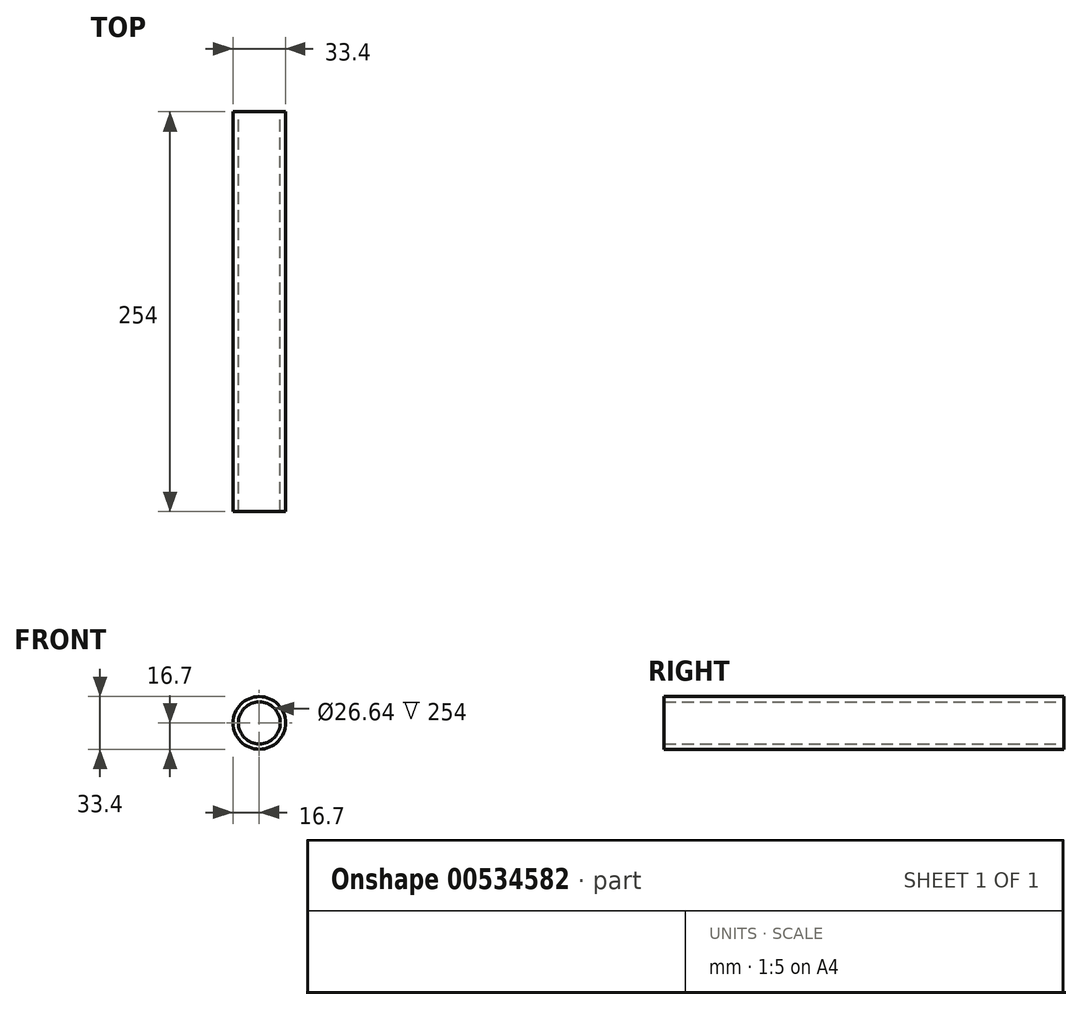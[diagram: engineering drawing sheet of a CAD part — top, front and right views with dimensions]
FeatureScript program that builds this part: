
annotation { "Feature Type Name" : "Feature", "Feature Type Description" : "" }
export const myFeature = defineFeature(function(context is Context, id is Id, definition is map)
    precondition{}
    {
        {
            var Q0;
            Q0=qCreatedBy(makeId("Front.planeOp"),FACE);
            var sketch = newSketch(context, id + "F0", { "sketchPlane" : qUnion([Q0])});
            skCircle(sketch, "E0", {"center": v(0, 0) * mm, "radius": 16.7 * mm});
            skCircle(sketch, "E1", {"center": v(0, 0) * mm, "radius": 13.32 * mm});
            skSolve(sketch);
        }
        {
            var Q0;
            Q0=makeQuery(id+"F0.imprint","IMPRINT",FACE,{"disambiguationData":[TD([[makeQuery(id+"F0.imprint","IMPRINT",EDGE,{"derivedFrom":sQuery(id+"F0.wireOp",EDGE,"E0")}),1.0]])]});
            extrude(context, id + "F1", {"entities" : qUnion([Q0]), "depth" : 254 * mm, "offsetDistance" : 25.4 * mm});
        }
    });
